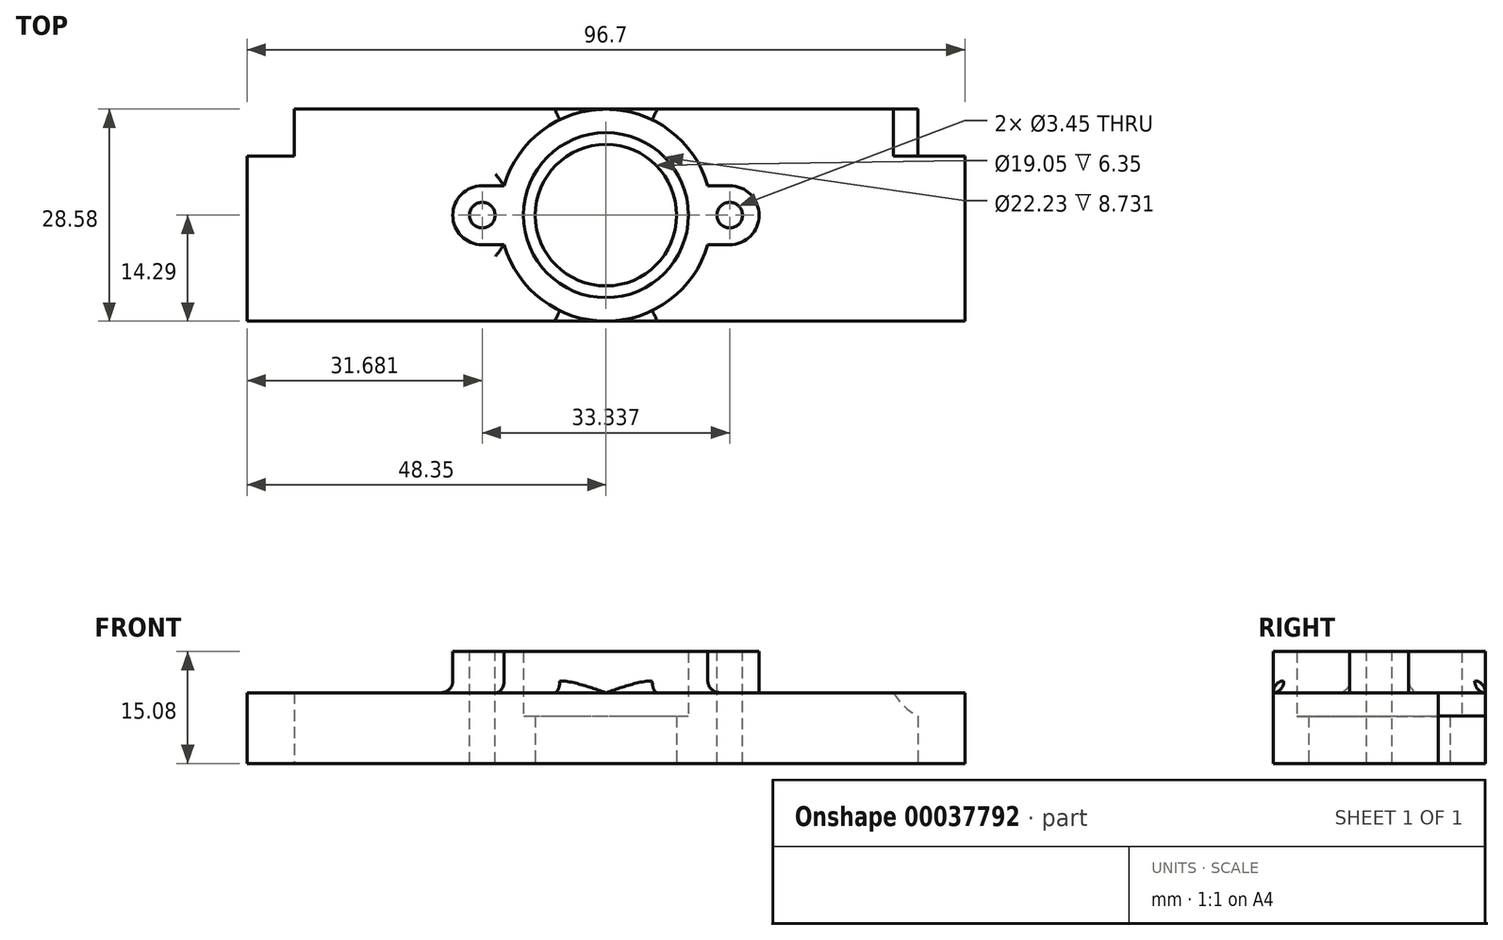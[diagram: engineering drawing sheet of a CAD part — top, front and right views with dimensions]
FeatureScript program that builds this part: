
annotation { "Feature Type Name" : "Feature", "Feature Type Description" : "" }
export const myFeature = defineFeature(function(context is Context, id is Id, definition is map)
    precondition{}
    {
        {
            var Q0;
            Q0=qCreatedBy(makeId("Top.planeOp"),FACE);
            var sketch = newSketch(context, id + "F0", { "sketchPlane" : qUnion([Q0])});
            skLineSegment(sketch, "E0.rect.bottom", {"start": v(42, 14.29) * mm, "end": v(-42, 14.29) * mm});
            skLineSegment(sketch, "E0.rect.top", {"start": v(48.35, -14.29) * mm, "end": v(-48.35, -14.29) * mm});
            skPoint(sketch, "E0.rect.middle", {"position": v(0, 0) * mm});
            skLineSegment(sketch, "E1", {"start": v(42, 14.29) * mm, "end": v(42, 7.94) * mm});
            skLineSegment(sketch, "E2.bottom", {"start": v(42, 7.94) * mm, "end": v(48.35, 7.94) * mm});
            skLineSegment(sketch, "E2.right", {"start": v(48.35, 7.94) * mm, "end": v(48.35, -14.29) * mm});
            skLineSegment(sketch, "E3", {"start": v(-42, 14.29) * mm, "end": v(-42, 7.94) * mm});
            skLineSegment(sketch, "E4.bottom", {"start": v(-42, 7.94) * mm, "end": v(-48.35, 7.94) * mm});
            skLineSegment(sketch, "E4.right", {"start": v(-48.35, 7.94) * mm, "end": v(-48.35, -14.29) * mm});
            skCircle(sketch, "E5", {"center": v(0, 0) * mm, "radius": 9.53 * mm});
            skLineSegment(sketch, "E6", {"start": v(0, -14.29) * mm, "end": v(0, 14.29) * mm, "construction": true});
            skSolve(sketch);
        }
        {
            var Q0;
            Q0 = qSketchRegion(id + "F0", true);
            extrude(context, id + "F1", {"entities" : qUnion([Q0]), "depth" : 9.52 * mm});
        }
        {
            var Q0;
            Q0=makeQuery(id+"F1.opExtrude","CAP_FACE",FACE,{"disambiguationData":[OSD([sQuery(id+"F0.wireOp",EDGE,"E0.rect.bottom"),sQuery(id+"F0.wireOp",EDGE,"E0.rect.top"),sQuery(id+"F0.wireOp",EDGE,"E1"),sQuery(id+"F0.wireOp",EDGE,"07fd7381-d756-40a0-9d22-78696dacdfad"),sQuery(id+"F0.wireOp",EDGE,"E2.bottom"),sQuery(id+"F0.wireOp",EDGE,"E2.top"),sQuery(id+"F0.wireOp",EDGE,"E2.right"),sQuery(id+"F0.wireOp",EDGE,"E3"),sQuery(id+"F0.wireOp",EDGE,"fed49cc1-aa32-4793-b533-85ae2eeac890"),sQuery(id+"F0.wireOp",EDGE,"E4.bottom"),sQuery(id+"F0.wireOp",EDGE,"E4.top"),sQuery(id+"F0.wireOp",EDGE,"E4.right"),sQuery(id+"F0.wireOp",EDGE,"E5")])],"isStart":false});
            var sketch = newSketch(context, id + "F2", { "sketchPlane" : qUnion([Q0])});
            skCircle(sketch, "E7", {"center": v(0, 0) * mm, "radius": 11.11 * mm});
            skLineSegment(sketch, "E8", {"start": v(-16.67, 0) * mm, "end": v(16.67, 0) * mm, "construction": true});
            skArc(sketch, "E9", {"start": v(13.73, 3.97) * mm, "mid": v(0, 14.29) * mm, "end": v(-13.73, 3.97) * mm});
            skArc(sketch, "E10", {"start": v(-13.73, -3.97) * mm, "mid": v(0, -14.29) * mm, "end": v(13.73, -3.97) * mm});
            skLineSegment(sketch, "E11", {"start": v(-16.67, 3.97) * mm, "end": v(-16.67, -3.97) * mm, "construction": true});
            skLineSegment(sketch, "E12", {"start": v(16.67, 3.97) * mm, "end": v(16.67, -3.97) * mm, "construction": true});
            skLineSegment(sketch, "E13", {"start": v(16.67, -3.97) * mm, "end": v(13.73, -3.97) * mm});
            skLineSegment(sketch, "E14", {"start": v(16.67, 3.97) * mm, "end": v(13.73, 3.97) * mm});
            skLineSegment(sketch, "E15", {"start": v(-16.67, -3.97) * mm, "end": v(-13.73, -3.97) * mm});
            skLineSegment(sketch, "E16", {"start": v(-16.67, 3.97) * mm, "end": v(-13.73, 3.97) * mm});
            skArc(sketch, "E17", {"start": v(-16.67, 3.97) * mm, "mid": v(-20.64, 0) * mm, "end": v(-16.67, -3.97) * mm});
            skArc(sketch, "E18", {"start": v(16.67, -3.97) * mm, "mid": v(20.64, 0) * mm, "end": v(16.67, 3.97) * mm});
            skSolve(sketch);
        }
        {
            var Q0;
            Q0 = qSketchRegion(id + "F2", true);
            extrude(context, id + "F3", {"entities" : qUnion([Q0]), "operationType" : NewBodyOperationType.ADD, "depth" : 5.56 * mm});
        }
        {
            var Q0;
            Q0=makeQuery(id+"F3.opExtrude","CAP_EDGE",EDGE,{"disambiguationData":[OSD([sQuery(id+"F2.wireOp",EDGE,"E9")])],"isStart":true});
            var Q1;
            Q1=makeQuery(id+"F3.opExtrude","CAP_EDGE",EDGE,{"disambiguationData":[OSD([sQuery(id+"F2.wireOp",EDGE,"E16")])],"isStart":true});
            var Q2;
            Q2=makeQuery(id+"F3.opExtrude","CAP_EDGE",EDGE,{"disambiguationData":[OSD([sQuery(id+"F2.wireOp",EDGE,"E17")])],"isStart":true});
            var Q3;
            Q3=makeQuery(id+"F3.opExtrude","CAP_EDGE",EDGE,{"disambiguationData":[OSD([sQuery(id+"F2.wireOp",EDGE,"E14")])],"isStart":true});
            var Q4;
            Q4=makeQuery(id+"F3.opExtrude","CAP_EDGE",EDGE,{"disambiguationData":[OSD([sQuery(id+"F2.wireOp",EDGE,"E18")])],"isStart":true});
            var Q5;
            Q5=makeQuery(id+"F3.opExtrude","CAP_EDGE",EDGE,{"disambiguationData":[OSD([sQuery(id+"F2.wireOp",EDGE,"E13")])],"isStart":true});
            var Q6;
            Q6=makeQuery(id+"F3.opExtrude","CAP_EDGE",EDGE,{"disambiguationData":[OSD([sQuery(id+"F2.wireOp",EDGE,"E10")])],"isStart":true});
            var Q7;
            Q7=makeQuery(id+"F3.opExtrude","CAP_EDGE",EDGE,{"disambiguationData":[OSD([sQuery(id+"F2.wireOp",EDGE,"E15")])],"isStart":true});
            fillet(context, id + "F4", {"entities" : qUnion([Q0, Q1, Q2, Q3, Q4, Q5, Q6, Q7]), "radius" : 1.59 * mm, "tangentPropagation" : true, "allowEdgeOverflow" : false});
        }
        {
            var Q0;
            Q0=makeQuery(id+"F3.opExtrude","CAP_FACE",FACE,{"disambiguationData":[OSD([sQuery(id+"F2.wireOp",EDGE,"E7"),sQuery(id+"F2.wireOp",EDGE,"E9"),sQuery(id+"F2.wireOp",EDGE,"E10"),sQuery(id+"F2.wireOp",EDGE,"E13"),sQuery(id+"F2.wireOp",EDGE,"E14"),sQuery(id+"F2.wireOp",EDGE,"E15"),sQuery(id+"F2.wireOp",EDGE,"E16"),sQuery(id+"F2.wireOp",EDGE,"E17"),sQuery(id+"F2.wireOp",EDGE,"E18")])],"isStart":false});
            var sketch = newSketch(context, id + "F5", { "sketchPlane" : qUnion([Q0])});
            skCircle(sketch, "E19", {"center": v(16.67, 0) * mm, "radius": 1.73 * mm});
            skCircle(sketch, "E20", {"center": v(-16.67, 0) * mm, "radius": 1.73 * mm});
            skSolve(sketch);
        }
        {
            var Q0;
            Q0 = qSketchRegion(id + "F5", true);
            var Q1;
            Q1=makeQuery(id+"F1.opExtrude","CAP_FACE",FACE,{"disambiguationData":[OSD([sQuery(id+"F0.wireOp",EDGE,"E0.rect.bottom"),sQuery(id+"F0.wireOp",EDGE,"E0.rect.top"),sQuery(id+"F0.wireOp",EDGE,"E1"),sQuery(id+"F0.wireOp",EDGE,"07fd7381-d756-40a0-9d22-78696dacdfad"),sQuery(id+"F0.wireOp",EDGE,"E2.bottom"),sQuery(id+"F0.wireOp",EDGE,"E2.top"),sQuery(id+"F0.wireOp",EDGE,"E2.right"),sQuery(id+"F0.wireOp",EDGE,"E3"),sQuery(id+"F0.wireOp",EDGE,"fed49cc1-aa32-4793-b533-85ae2eeac890"),sQuery(id+"F0.wireOp",EDGE,"E4.bottom"),sQuery(id+"F0.wireOp",EDGE,"E4.top"),sQuery(id+"F0.wireOp",EDGE,"E4.right"),sQuery(id+"F0.wireOp",EDGE,"E5")])],"isStart":true});
            extrude(context, id + "F6", {"entities" : qUnion([Q0]), "operationType" : NewBodyOperationType.REMOVE, "endBound" : BoundingType.UP_TO_SURFACE, "oppositeDirection" : true, "endBoundEntityFace" : qUnion([Q1]), "depth" : 25.4 * mm});
        }
        {
            var Q0;
            {var subQ0=sQuery(id+"F0.wireOp",EDGE,"E5");Q0=makeQuery(id+"F3.boolean.opBoolean","SPLIT",FACE,{"disambiguationData":[TD([makeQuery(id+"F1.opExtrude","SWEPT_FACE",FACE,{"disambiguationData":[OSD([subQ0])]})])],"derivedFrom":makeQuery(id+"F1.opExtrude","CAP_FACE",FACE,{"disambiguationData":[OSD([sQuery(id+"F0.wireOp",EDGE,"E0.rect.bottom"),sQuery(id+"F0.wireOp",EDGE,"E0.rect.top"),sQuery(id+"F0.wireOp",EDGE,"E1"),sQuery(id+"F0.wireOp",EDGE,"E2.bottom"),sQuery(id+"F0.wireOp",EDGE,"E2.right"),sQuery(id+"F0.wireOp",EDGE,"E3"),sQuery(id+"F0.wireOp",EDGE,"E4.bottom"),sQuery(id+"F0.wireOp",EDGE,"E4.right"),subQ0])],"isStart":false})});}
            extrude(context, id + "F7", {"entities" : qUnion([Q0]), "operationType" : NewBodyOperationType.REMOVE, "oppositeDirection" : true, "depth" : 3.17 * mm});
        }
        {
            var Q0;
            Q0=makeQuery(id+"F1.opExtrude","SWEPT_FACE",FACE,{"disambiguationData":[OSD([sQuery(id+"F0.wireOp",EDGE,"E0.rect.bottom")])]});
            var sketch = newSketch(context, id + "F8", { "sketchPlane" : qUnion([Q0])});
            skLineSegment(sketch, "E21.bottom", {"start": v(-42, 9.53) * mm, "end": v(-38.7, 9.53) * mm});
            skLineSegment(sketch, "E21.top", {"start": v(-42, 6.36) * mm, "end": v(-38.7, 6.36) * mm, "construction": true});
            skLineSegment(sketch, "E21.left", {"start": v(-42, 9.53) * mm, "end": v(-42, 6.36) * mm});
            skLineSegment(sketch, "E21.right", {"start": v(-38.7, 9.53) * mm, "end": v(-38.7, 6.36) * mm, "construction": true});
            skArc(sketch, "E22", {"start": v(-42, 6.36) * mm, "mid": v(-40.16, 7.74) * mm, "end": v(-38.7, 9.52) * mm});
            skSolve(sketch);
        }
        {
            var Q0;
            Q0 = qSketchRegion(id + "F8", true);
            var Q1;
            Q1=makeQuery(id+"F1.opExtrude","SWEPT_FACE",FACE,{"disambiguationData":[OSD([sQuery(id+"F0.wireOp",EDGE,"E2.bottom")])]});
            extrude(context, id + "F9", {"entities" : qUnion([Q0]), "operationType" : NewBodyOperationType.REMOVE, "endBound" : BoundingType.UP_TO_SURFACE, "oppositeDirection" : true, "endBoundEntityFace" : qUnion([Q1]), "depth" : 25.4 * mm});
        }
    });
